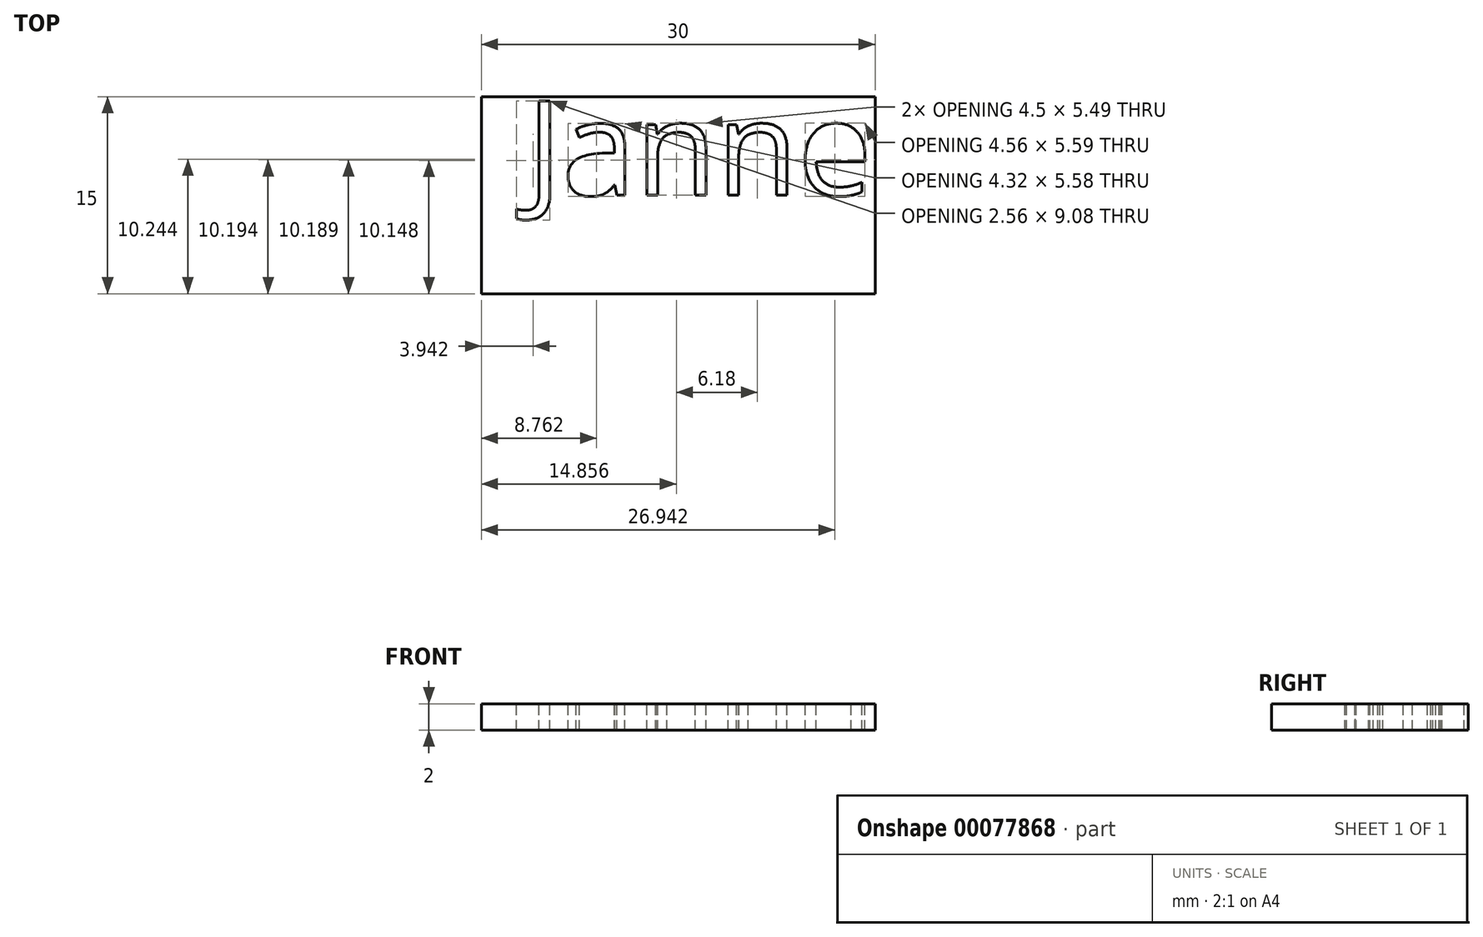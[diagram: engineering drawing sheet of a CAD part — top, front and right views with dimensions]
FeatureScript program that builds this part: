
annotation { "Feature Type Name" : "Feature", "Feature Type Description" : "" }
export const myFeature = defineFeature(function(context is Context, id is Id, definition is map)
    precondition{}
    {
        {
            var Q0;
            Q0=qCreatedBy(makeId("Top.planeOp"),FACE);
            var Q1;
            Q1=qCreatedBy(makeId("Top.planeOp"),FACE);
            var sketch = newSketch(context, id + "F0", { "sketchPlane" : qUnion([Q0, Q1])});
            skLineSegment(sketch, "E0", {"start": v(0, 0) * mm, "end": v(-30, 0) * mm});
            skLineSegment(sketch, "E1", {"start": v(-30, 0) * mm, "end": v(-30, 15) * mm});
            skLineSegment(sketch, "E2", {"start": v(-30, 15) * mm, "end": v(0, 15) * mm});
            skLineSegment(sketch, "E3", {"start": v(0, 15) * mm, "end": v(0, 0) * mm});
            skText(sketch, "E4", { "text": "Janne", "fontName": "OpenSans-Regular.ttf"});
            const initialGuessF0  = {"E4": [-0.02655, 0.0075, 1, 0, 0.00725]};
            skSetInitialGuess(sketch, initialGuessF0);
            skSolve(sketch);
        }
        {
            var Q0;
            Q0=makeQuery(id+"F0.imprint","IMPRINT",FACE,{"disambiguationData":[TD([[makeQuery(id+"F0.imprint","IMPRINT",EDGE,{"derivedFrom":sQuery(id+"F0.wireOp",EDGE,"E0")}),-1.0]])]});
            extrude(context, id + "F1", {"entities" : qUnion([Q0]), "oppositeDirection" : true, "depth" : 2 * mm});
        }
    });
